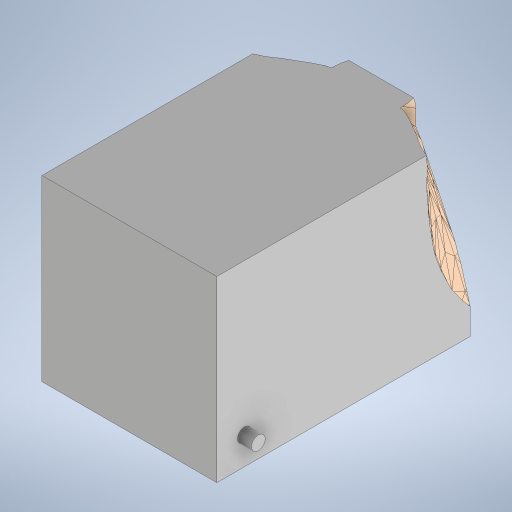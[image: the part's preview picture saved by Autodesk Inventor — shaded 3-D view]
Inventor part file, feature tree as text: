
AUTODESK INVENTOR PART (.ipt)
format: ipt  version: 2024 (Build 280153000, 153)  size: 10,670,080 bytes
history: native  units: mm
features: other x6, sketch x5, extrude x4, plane x2
ambient origin geometry x8: Origin, YZ Plane, XZ Plane, XY Plane, X Axis, Y Axis, Z Axis, Center Point
bodies: Body1 (feature_tree)
feature tree (17):
  other  "M.ipt"
  plane  "Plano de trabajo1"
  extrude  "Extrusión1"  [1 undecoded]
  other  "Combinar1"
  sketch  "Boceto3"  dims[d2=550.0mm d3=520.0mm]
  sketch  "Boceto4"  dims[d4=550.0mm d5=0.0mm d6=129.8482mm]
  plane  "Plano de trabajo2"
  sketch  "Boceto5"  dims[d17=180.0mm d18=180.0mm]
  extrude  "Extrusión2"  Depth=520.0mm
  extrude  "Extrusión3"  Depth=129.8482mm
  extrude  "Extrusión4"  Depth=180.0mm
  other  "Sólido1::M.ipt"
  other  "OperaciónIdentificador1"
  sketch  "Boceto1"  dims[d0=25.0mm d1=-365.0mm]
  other  "Sólido2"
  sketch  "Boceto6"  dims[d22=326.0mm d23=180.0mm d24=180.0mm d25=180.0mm d26=10.0mm d27=0.0mm d28=1000.0mm d29=0.0mm d30=30.0mm d31=30.0mm d32=15.0mm d33=15.0mm d34=205.0mm d35=0.0mm d36=0.0mm d14=0.5mm d15=0.872665mm d16=0.5mm d19=0.5mm d20=0.872665mm d21=0.5mm]
  other  "Sólido1"
note: 1 required parameter value undecoded (feature->parameter linkage not recoverable at this tier; creation-order binding heuristic only, values carry confidence <= 0.55)
